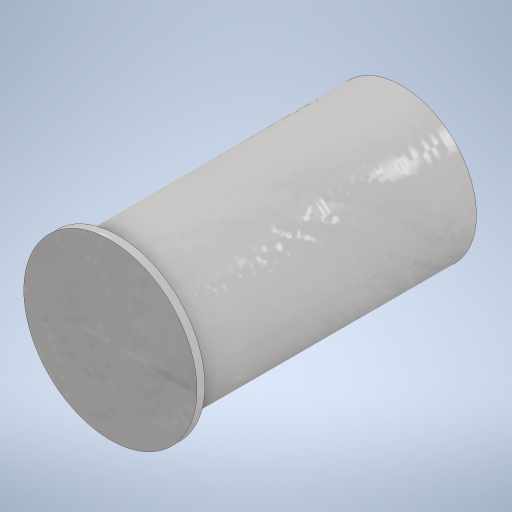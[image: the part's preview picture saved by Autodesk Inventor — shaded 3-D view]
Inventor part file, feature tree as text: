
AUTODESK INVENTOR PART (.ipt)
format: ipt  version: 2024.2 (Build 282272000, 272)  size: 254,976 bytes
history: native  units: mm
features: extrude x2, sketch x2
ambient origin geometry x8: Origin, YZ Plane, XZ Plane, XY Plane, X Axis, Y Axis, Z Axis, Center Point
bodies: Solid1 (feature_tree)
feature tree (4):
  extrude  "Extrusion1"  Depth=18.0mm TaperAngle=0.0deg
  extrude  "Extrusion2"  Depth=0.5mm TaperAngle=0.0deg
  sketch  "Sketch1"  dims[d0=9.5mm d2=18.0mm d3=0.0mm]
  sketch  "Sketch2"  dims[d4=11.0mm d5=0.5mm d6=0.0mm]
